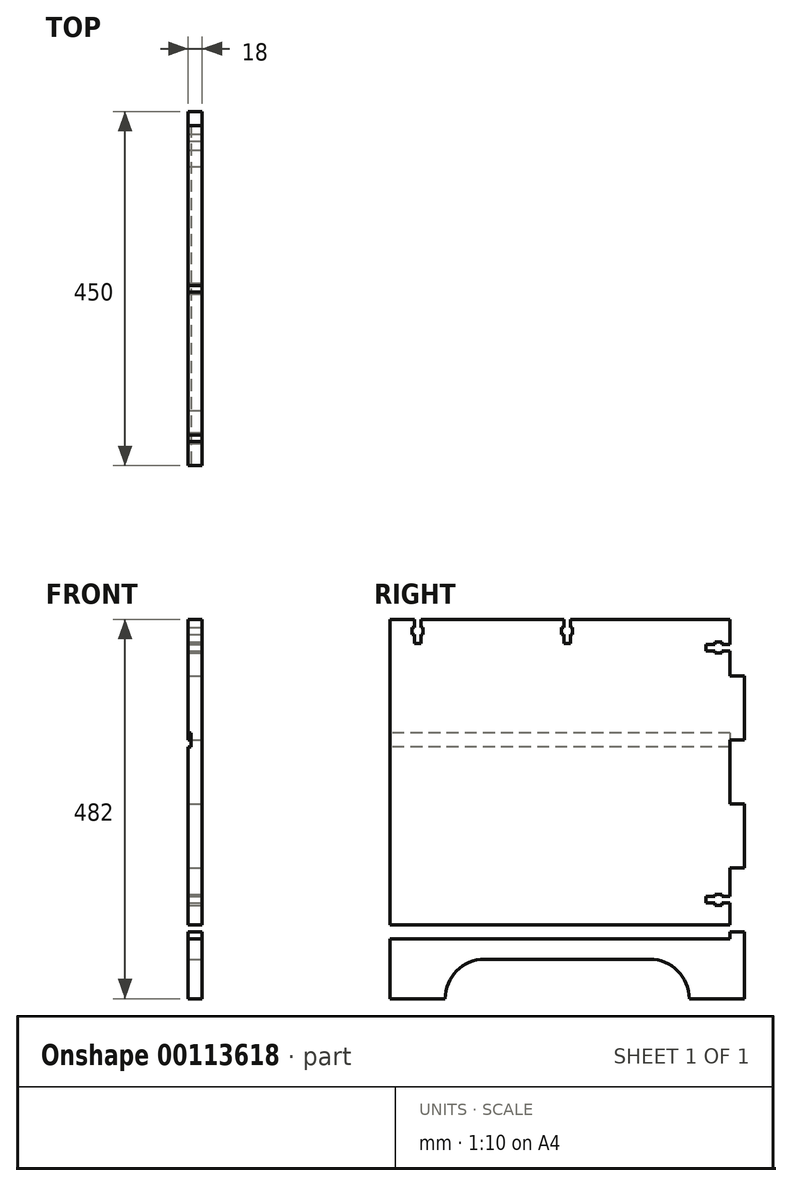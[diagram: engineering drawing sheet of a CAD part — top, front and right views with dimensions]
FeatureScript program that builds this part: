
annotation { "Feature Type Name" : "Feature", "Feature Type Description" : "" }
export const myFeature = defineFeature(function(context is Context, id is Id, definition is map)
    precondition{}
    {
        {
            assignVariable(context, id + "F0", {"name" : "dicke", "anyValue" : 18});
        }
        {
            assignVariable(context, id + "F1", {"name" : "einschub", "anyValue" : 4});
        }
        {
            var Q0;
            Q0=qCreatedBy(makeId("Right.planeOp"),FACE);
            var sketch = newSketch(context, id + "F2", { "sketchPlane" : qUnion([Q0])});
            skLineSegment(sketch, "E0.bottom", {"start": v(225, 250) * mm, "end": v(-225, 250) * mm});
            skLineSegment(sketch, "E0.top", {"start": v(225, -250) * mm, "end": v(-225, -250) * mm, "construction": true});
            skLineSegment(sketch, "E0.left", {"start": v(225, 250) * mm, "end": v(225, -250) * mm, "construction": true});
            skLineSegment(sketch, "E0.right", {"start": v(-225, 250) * mm, "end": v(-225, -250) * mm, "construction": true});
            skPoint(sketch, "E0.middle", {"position": v(0, 0) * mm});
            skLineSegment(sketch, "E1", {"start": v(-225, 232) * mm, "end": v(225, 232) * mm});
            skLineSegment(sketch, "E2", {"start": v(-225, -200) * mm, "end": v(225, -200) * mm, "construction": true});
            skLineSegment(sketch, "E3", {"start": v(-225, -250) * mm, "end": v(-155, -250) * mm});
            skLineSegment(sketch, "E4", {"start": v(225, -250) * mm, "end": v(155, -250) * mm});
            skArc(sketch, "E5", {"start": v(-105, -200) * mm, "mid": v(-140.36, -214.64) * mm, "end": v(-155, -250) * mm});
            skArc(sketch, "E6", {"start": v(155, -250) * mm, "mid": v(140.36, -214.64) * mm, "end": v(105, -200) * mm});
            skLineSegment(sketch, "E7", {"start": v(-105, -200) * mm, "end": v(105, -200) * mm});
            skLineSegment(sketch, "E8", {"start": v(-225, -250) * mm, "end": v(-225, 232) * mm, "construction": true});
            skLineSegment(sketch, "E9", {"start": v(-225, -165) * mm, "end": v(225, -165) * mm, "construction": true});
            skLineSegment(sketch, "E10.bottom", {"start": v(225, -156) * mm, "end": v(207, -156) * mm, "construction": true});
            skLineSegment(sketch, "E10.top", {"start": v(225, -174) * mm, "end": v(207, -174) * mm, "construction": true});
            skLineSegment(sketch, "E10.left", {"start": v(225, -156) * mm, "end": v(225, -174) * mm, "construction": true});
            skLineSegment(sketch, "E10.right", {"start": v(-225, -156) * mm, "end": v(-225, -174) * mm, "construction": true});
            skPoint(sketch, "E10.middle", {"position": v(0, -165) * mm});
            skLineSegment(sketch, "E11.0.1.0", {"start": v(225, -74.8) * mm, "end": v(-225, -74.8) * mm, "construction": true});
            skLineSegment(sketch, "E11.0.1.1", {"start": v(-225, -83.8) * mm, "end": v(225, -83.8) * mm, "construction": true});
            skLineSegment(sketch, "E11.0.1.2", {"start": v(225, -92.8) * mm, "end": v(-225, -92.8) * mm, "construction": true});
            skLineSegment(sketch, "E11.0.2.0", {"start": v(225, 6.4) * mm, "end": v(-225, 6.4) * mm, "construction": true});
            skLineSegment(sketch, "E11.0.2.1", {"start": v(-225, -2.6) * mm, "end": v(225, -2.6) * mm, "construction": true});
            skLineSegment(sketch, "E11.0.2.2", {"start": v(225, -11.6) * mm, "end": v(-225, -11.6) * mm, "construction": true});
            skLineSegment(sketch, "E11.0.3.0", {"start": v(225, 87.6) * mm, "end": v(207, 87.6) * mm, "construction": true});
            skLineSegment(sketch, "E11.0.3.1", {"start": v(-225, 78.6) * mm, "end": v(225, 78.6) * mm, "construction": true});
            skLineSegment(sketch, "E11.0.3.2", {"start": v(225, 69.6) * mm, "end": v(207, 69.6) * mm, "construction": true});
            skLineSegment(sketch, "E11.direction1", {"start": v(-225, -174) * mm, "end": v(-200, -174) * mm, "construction": true});
            skLineSegment(sketch, "E11.direction2", {"start": v(-225, -174) * mm, "end": v(-225, -92.8) * mm, "construction": true});
            skLineSegment(sketch, "E12.0.0.4", {"start": v(225, 168.8) * mm, "end": v(-225, 168.8) * mm, "construction": true});
            skLineSegment(sketch, "E12.3.0.4", {"start": v(-225, 159.8) * mm, "end": v(225, 159.8) * mm, "construction": true});
            skLineSegment(sketch, "E12.6.0.4", {"start": v(225, 150.8) * mm, "end": v(-225, 150.8) * mm, "construction": true});
            skLineSegment(sketch, "E13.3.0.5", {"start": v(-225, 241) * mm, "end": v(225, 241) * mm, "construction": true});
            skLineSegment(sketch, "E13.6.0.5", {"start": v(225, 232) * mm, "end": v(-225, 232) * mm, "construction": true});
            skLineSegment(sketch, "E14", {"start": v(207, -250) * mm, "end": v(207, -174) * mm, "construction": true});
            skLineSegment(sketch, "E15", {"start": v(207, 232) * mm, "end": v(207, 159.8) * mm});
            skLineSegment(sketch, "E16", {"start": v(207, 159.8) * mm, "end": v(225, 159.8) * mm});
            skLineSegment(sketch, "E17", {"start": v(225, 159.8) * mm, "end": v(225, 78.6) * mm});
            skLineSegment(sketch, "E18", {"start": v(225, 78.6) * mm, "end": v(207, 78.6) * mm});
            skLineSegment(sketch, "E19", {"start": v(207, 78.6) * mm, "end": v(207, -2.6) * mm});
            skLineSegment(sketch, "E20", {"start": v(207, -2.6) * mm, "end": v(225, -2.6) * mm});
            skLineSegment(sketch, "E21", {"start": v(225, -2.6) * mm, "end": v(225, -83.8) * mm});
            skLineSegment(sketch, "E22", {"start": v(225, -83.8) * mm, "end": v(207, -83.8) * mm});
            skLineSegment(sketch, "E23", {"start": v(225, -165) * mm, "end": v(225, -250) * mm});
            skLineSegment(sketch, "E24", {"start": v(-225, -250) * mm, "end": v(-225, 232) * mm});
            skLineSegment(sketch, "E25", {"start": v(-225, 232) * mm, "end": v(207, 232) * mm});
            skLineSegment(sketch, "E26", {"start": v(216, 250) * mm, "end": v(216, -250) * mm, "construction": true});
            skLineSegment(sketch, "E27", {"start": v(-190, 250) * mm, "end": v(-190, -250) * mm, "construction": true});
            skPoint(sketch, "E28", {"position": v(-190, -165) * mm});
            skPoint(sketch, "E29", {"position": v(-190, -83.8) * mm});
            skPoint(sketch, "E30", {"position": v(-190, -2.6) * mm});
            skPoint(sketch, "E31", {"position": v(-190, 78.6) * mm});
            skPoint(sketch, "E32", {"position": v(-190, 159.8) * mm});
            skLineSegment(sketch, "E33", {"start": v(207, 195.9) * mm, "end": v(176, 195.9) * mm, "construction": true});
            skPoint(sketch, "E34", {"position": v(196.5, 195.9) * mm});
            skLineSegment(sketch, "E35", {"start": v(176, 200.1) * mm, "end": v(176, 191.7) * mm});
            skLineSegment(sketch, "E36", {"start": v(176, 200.1) * mm, "end": v(177, 200.1) * mm});
            skLineSegment(sketch, "E37", {"start": v(187.5, 200.1) * mm, "end": v(187.5, 202.9) * mm});
            skLineSegment(sketch, "E38", {"start": v(187.5, 202.9) * mm, "end": v(196.5, 202.9) * mm});
            skLineSegment(sketch, "E39", {"start": v(196.5, 202.9) * mm, "end": v(196.5, 200.1) * mm});
            skLineSegment(sketch, "E40", {"start": v(196.5, 200.1) * mm, "end": v(207, 200.1) * mm});
            skLineSegment(sketch, "E41", {"start": v(176, 191.7) * mm, "end": v(177, 191.7) * mm});
            skLineSegment(sketch, "E42", {"start": v(187.5, 191.7) * mm, "end": v(187.5, 188.9) * mm});
            skLineSegment(sketch, "E43", {"start": v(187.5, 188.9) * mm, "end": v(196.5, 188.9) * mm});
            skLineSegment(sketch, "E44", {"start": v(196.5, 188.9) * mm, "end": v(196.5, 191.7) * mm});
            skLineSegment(sketch, "E45", {"start": v(196.5, 191.7) * mm, "end": v(207, 191.7) * mm});
            skLineSegment(sketch, "E46.0.1.0", {"start": v(196.5, -120.2) * mm, "end": v(207, -120.2) * mm});
            skLineSegment(sketch, "E46.0.1.1", {"start": v(187.5, -117.4) * mm, "end": v(196.5, -117.4) * mm});
            skLineSegment(sketch, "E46.0.1.2", {"start": v(176, -120.2) * mm, "end": v(176, -128.6) * mm});
            skPoint(sketch, "E46.0.1.3", {"position": v(196.5, -124.4) * mm});
            skLineSegment(sketch, "E46.0.1.4", {"start": v(187.5, -131.4) * mm, "end": v(196.5, -131.4) * mm});
            skLineSegment(sketch, "E46.0.1.5", {"start": v(176, -128.6) * mm, "end": v(187.5, -128.6) * mm});
            skLineSegment(sketch, "E46.0.1.6", {"start": v(187.5, -120.2) * mm, "end": v(187.5, -117.4) * mm});
            skLineSegment(sketch, "E46.0.1.7", {"start": v(196.5, -131.4) * mm, "end": v(196.5, -128.6) * mm});
            skLineSegment(sketch, "E46.0.1.8", {"start": v(176, -120.2) * mm, "end": v(187.5, -120.2) * mm});
            skLineSegment(sketch, "E46.0.1.9", {"start": v(196.5, -117.4) * mm, "end": v(196.5, -120.2) * mm});
            skLineSegment(sketch, "E46.0.1.10", {"start": v(187.5, -128.6) * mm, "end": v(187.5, -131.4) * mm});
            skLineSegment(sketch, "E46.0.1.11", {"start": v(196.5, -128.6) * mm, "end": v(207, -128.6) * mm});
            skLineSegment(sketch, "E46.0.1.12", {"start": v(207, -124.4) * mm, "end": v(176, -124.4) * mm, "construction": true});
            skLineSegment(sketch, "E46.direction1", {"start": v(187.5, 188.9) * mm, "end": v(205, 188.9) * mm, "construction": true});
            skLineSegment(sketch, "E46.direction2", {"start": v(187.5, 188.9) * mm, "end": v(187.5, -131.4) * mm, "construction": true});
            skLineSegment(sketch, "E47", {"start": v(-190, 232) * mm, "end": v(-190, 201) * mm, "construction": true});
            skPoint(sketch, "E48", {"position": v(-190, 221.5) * mm});
            skLineSegment(sketch, "E49", {"start": v(-194.2, 201) * mm, "end": v(-185.8, 201) * mm});
            skLineSegment(sketch, "E50", {"start": v(-194.2, 201) * mm, "end": v(-194.2, 202) * mm});
            skLineSegment(sketch, "E51", {"start": v(-194.2, 212.5) * mm, "end": v(-197, 212.5) * mm});
            skLineSegment(sketch, "E52", {"start": v(-197, 212.5) * mm, "end": v(-197, 221.5) * mm});
            skLineSegment(sketch, "E53", {"start": v(-197, 221.5) * mm, "end": v(-194.2, 221.5) * mm});
            skLineSegment(sketch, "E54", {"start": v(-194.2, 221.5) * mm, "end": v(-194.2, 232) * mm});
            skLineSegment(sketch, "E55", {"start": v(-185.8, 201) * mm, "end": v(-185.8, 202) * mm});
            skLineSegment(sketch, "E56", {"start": v(-185.8, 212.5) * mm, "end": v(-183, 212.5) * mm});
            skLineSegment(sketch, "E57", {"start": v(-183, 212.5) * mm, "end": v(-183, 221.5) * mm});
            skLineSegment(sketch, "E58", {"start": v(-183, 221.5) * mm, "end": v(-185.8, 221.5) * mm});
            skLineSegment(sketch, "E59", {"start": v(-185.8, 221.5) * mm, "end": v(-185.8, 232) * mm});
            skLineSegment(sketch, "E60.1.0.0", {"start": v(7, 212.5) * mm, "end": v(7, 221.5) * mm});
            skLineSegment(sketch, "E60.1.0.1", {"start": v(-7, 212.5) * mm, "end": v(-7, 221.5) * mm});
            skPoint(sketch, "E60.1.0.2", {"position": v(0, 221.5) * mm});
            skLineSegment(sketch, "E60.1.0.3", {"start": v(-4.2, 201) * mm, "end": v(4.2, 201) * mm});
            skLineSegment(sketch, "E60.1.0.4", {"start": v(-7, 221.5) * mm, "end": v(-4.2, 221.5) * mm});
            skLineSegment(sketch, "E60.1.0.5", {"start": v(4.2, 212.5) * mm, "end": v(7, 212.5) * mm});
            skLineSegment(sketch, "E60.1.0.6", {"start": v(4.2, 201) * mm, "end": v(4.2, 212.5) * mm});
            skLineSegment(sketch, "E60.1.0.7", {"start": v(-4.2, 212.5) * mm, "end": v(-7, 212.5) * mm});
            skLineSegment(sketch, "E60.1.0.8", {"start": v(7, 221.5) * mm, "end": v(4.2, 221.5) * mm});
            skLineSegment(sketch, "E60.1.0.9", {"start": v(-4.2, 201) * mm, "end": v(-4.2, 212.5) * mm});
            skLineSegment(sketch, "E60.1.0.10", {"start": v(-4.2, 221.5) * mm, "end": v(-4.2, 232) * mm});
            skLineSegment(sketch, "E60.1.0.11", {"start": v(0, 232) * mm, "end": v(0, 201) * mm, "construction": true});
            skLineSegment(sketch, "E60.1.0.12", {"start": v(4.2, 221.5) * mm, "end": v(4.2, 232) * mm});
            skLineSegment(sketch, "E60.direction1", {"start": v(-194.2, 201) * mm, "end": v(-4.2, 201) * mm, "construction": true});
            skLineSegment(sketch, "E61.left", {"start": v(-225, -156) * mm, "end": v(-225, -174) * mm});
            skLineSegment(sketch, "E62", {"start": v(-194.2, 202) * mm, "end": v(-194.2, 212.5) * mm});
            skLineSegment(sketch, "E63", {"start": v(-185.8, 202) * mm, "end": v(-185.8, 212.5) * mm});
            skLineSegment(sketch, "E64", {"start": v(-185.8, 232) * mm, "end": v(-185.8, 250) * mm, "construction": true});
            skLineSegment(sketch, "E65", {"start": v(-194.2, 232) * mm, "end": v(-194.2, 250) * mm, "construction": true});
            skLineSegment(sketch, "E66", {"start": v(207, 200.1) * mm, "end": v(225, 200.1) * mm, "construction": true});
            skLineSegment(sketch, "E67", {"start": v(207, 191.7) * mm, "end": v(225, 191.7) * mm, "construction": true});
            skLineSegment(sketch, "E68", {"start": v(177, 200.1) * mm, "end": v(187.5, 200.1) * mm});
            skLineSegment(sketch, "E69", {"start": v(177, 191.7) * mm, "end": v(187.5, 191.7) * mm});
            skPoint(sketch, "E70", {"position": v(0, 78.6) * mm});
            skLineSegment(sketch, "E71", {"start": v(225, 232) * mm, "end": v(225, -250) * mm});
            skLineSegment(sketch, "E72", {"start": v(207, -83.8) * mm, "end": v(207, -165) * mm});
            skLineSegment(sketch, "E73", {"start": v(207, -165) * mm, "end": v(225, -165) * mm});
            skLineSegment(sketch, "E74", {"start": v(207, -156) * mm, "end": v(-225, -156) * mm});
            skLineSegment(sketch, "E75", {"start": v(207, 87.6) * mm, "end": v(-225, 87.6) * mm});
            skLineSegment(sketch, "E76", {"start": v(207, -174) * mm, "end": v(207, -165) * mm});
            skLineSegment(sketch, "E77", {"start": v(207, -165) * mm, "end": v(207, -83.8) * mm});
            skLineSegment(sketch, "E78", {"start": v(207, -174) * mm, "end": v(-225, -174) * mm});
            skLineSegment(sketch, "E79", {"start": v(207, -83.8) * mm, "end": v(207, -2.6) * mm, "construction": true});
            skLineSegment(sketch, "E80", {"start": v(207, -2.6) * mm, "end": v(207, 69.6) * mm});
            skLineSegment(sketch, "E81", {"start": v(207, 69.6) * mm, "end": v(207, 87.6) * mm});
            skLineSegment(sketch, "E82", {"start": v(207, 69.6) * mm, "end": v(-225, 69.6) * mm});
            skLineSegment(sketch, "E83", {"start": v(207, 87.6) * mm, "end": v(207, 159.8) * mm, "construction": true});
            skLineSegment(sketch, "E84", {"start": v(207, 159.8) * mm, "end": v(207, 232) * mm});
            skSolve(sketch);
        }
        {
            var Q0;
            {var subQ4=sQuery(id+"F2.wireOp",EDGE,"E16");Q0=makeQuery(id+"F2.imprint","IMPRINT",FACE,{"disambiguationData":[TD([[makeQuery(id+"F2.imprint","IMPRINT",EDGE,{"derivedFrom":subQ4}),-1.0]])]});}
            var Q1;
            {var subQ0=sQuery(id+"F2.wireOp",EDGE,"E20");Q1=makeQuery(id+"F2.imprint","IMPRINT",FACE,{"disambiguationData":[TD([[makeQuery(id+"F2.imprint","IMPRINT",EDGE,{"derivedFrom":subQ0}),-1.0]])]});}
            var Q2;
            {var subQ4=sQuery(id+"F2.wireOp",EDGE,"E3");Q2=makeQuery(id+"F2.imprint","IMPRINT",FACE,{"disambiguationData":[TD([[makeQuery(id+"F2.imprint","IMPRINT",EDGE,{"derivedFrom":subQ4}),1.0]])]});}
            extrude(context, id + "F3", {"entities" : qUnion([Q0, Q1, Q2]), "oppositeDirection" : true, "depth" : (getVariable(context, 'dicke')) * mm});
        }
        {
            var Q0;
            {var subQ2=sQuery(id+"F2.wireOp",EDGE,"E75");Q0=makeQuery(id+"F2.imprint","IMPRINT",FACE,{"disambiguationData":[TD([[makeQuery(id+"F2.imprint","IMPRINT",EDGE,{"derivedFrom":subQ2}),1.0]])]});}
            var Q1;
            Q1=makeQuery(id+"F2.imprint","IMPRINT",FACE,{"disambiguationData":[TD([[makeQuery(id+"F2.imprint","IMPRINT",EDGE,{"derivedFrom":sQuery(id+"F2.wireOp",EDGE,"E61.left")}),1.0]])]});
            extrude(context, id + "F4", {"entities" : qUnion([Q0, Q1]), "operationType" : NewBodyOperationType.ADD, "oppositeDirection" : true, "depth" : (getVariable(context, 'dicke') - getVariable(context, 'einschub')) * mm});
        }
        {
            var Q0;
            Q0=sQuery(id+"F2.wireOp",VERTEX,"E31");
            var Q1;
            Q1=sQuery(id+"F2.wireOp",VERTEX,"E70");
            var Q2;
            Q2=sQuery(id+"F2.wireOp",VERTEX,"E10.middle");
            var Q3;
            Q3=sQuery(id+"F2.wireOp",VERTEX,"E28");
            var Q4;
            Q4=makeQuery(id+"F3.opExtrude","SWEPT_BODY",BODY,{"disambiguationData":[OSD([sQuery(id+"F2.wireOp",EDGE,"E3"),sQuery(id+"F2.wireOp",EDGE,"E4"),sQuery(id+"F2.wireOp",EDGE,"E5"),sQuery(id+"F2.wireOp",EDGE,"E6"),sQuery(id+"F2.wireOp",EDGE,"E7"),sQuery(id+"F2.wireOp",EDGE,"E24"),sQuery(id+"F2.wireOp",EDGE,"E71"),sQuery(id+"F2.wireOp",EDGE,"E73"),sQuery(id+"F2.wireOp",EDGE,"E76"),sQuery(id+"F2.wireOp",EDGE,"E78")])]});
            hole(context, id + "F5", {"style" : HoleStyle.C_BORE, "endStyle" : HoleEndStyle.THROUGH, "standardTappedOrClearance" : lookupTablePath({ "standard" : "ISO", "fit" : "Close", "size" : "M8", "type" : "Clearance" }), "standardBlindInLast" : lookupTablePath({ "fit" : "Close", "standard" : "ISO", "size" : "M8", "type" : "Clearance" }), "holeDiameter" : 8.4 * mm, "cBoreDiameter" : 14.25 * mm, "cBoreDepth" : 8 * mm, "startFromSketch" : true, "locations" : qUnion([Q0, Q1, Q2, Q3]), "scope" : qUnion([Q4]), "isTappedThrough" : true});
        }
    });
